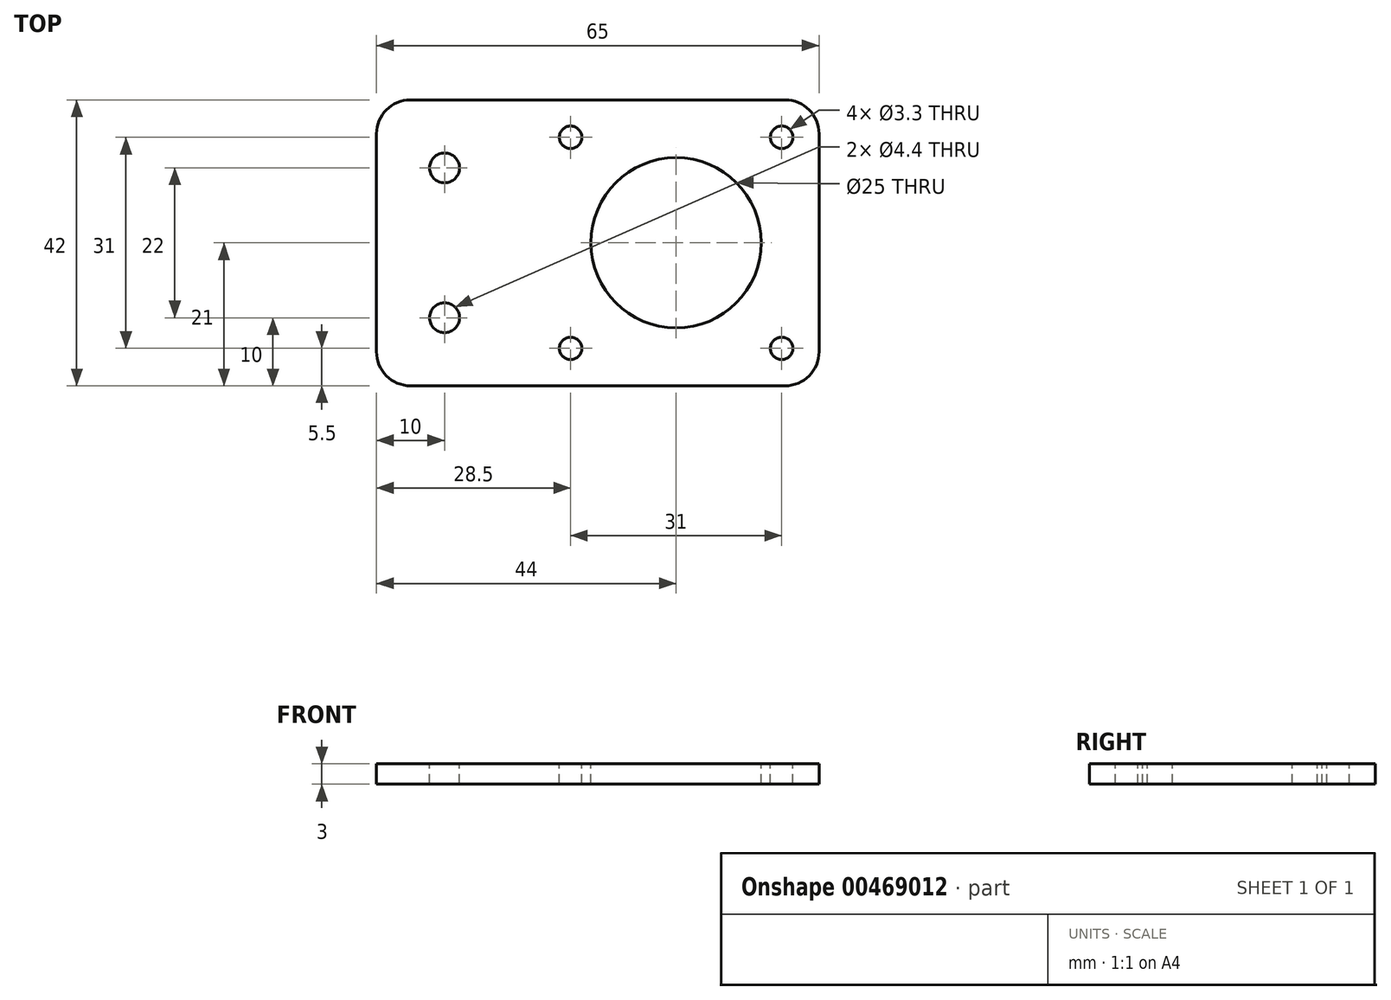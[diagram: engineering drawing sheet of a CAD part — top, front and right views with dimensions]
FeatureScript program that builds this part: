
annotation { "Feature Type Name" : "Feature", "Feature Type Description" : "" }
export const myFeature = defineFeature(function(context is Context, id is Id, definition is map)
    precondition{}
    {
        {
            var Q0;
            Q0=qCreatedBy(makeId("Top.planeOp"),FACE);
            var sketch = newSketch(context, id + "F0", { "sketchPlane" : qUnion([Q0])});
            skLineSegment(sketch, "E0.bottom", {"start": v(0, 0) * mm, "end": v(65, 0) * mm});
            skLineSegment(sketch, "E0.top", {"start": v(0, -42) * mm, "end": v(65, -42) * mm});
            skLineSegment(sketch, "E0.left", {"start": v(0, 0) * mm, "end": v(0, -42) * mm});
            skLineSegment(sketch, "E0.right", {"start": v(65, 0) * mm, "end": v(65, -42) * mm});
            skSolve(sketch);
        }
        {
            var Q0;
            Q0=makeQuery(id+"F0.imprint","IMPRINT",FACE,{"disambiguationData":[TD([[makeQuery(id+"F0.imprint","IMPRINT",EDGE,{"derivedFrom":sQuery(id+"F0.wireOp",EDGE,"E0.bottom")}),-1.0]])]});
            extrude(context, id + "F1", {"entities" : qUnion([Q0]), "depth" : 3 * mm});
        }
        {
            var Q0;
            Q0=makeQuery(id+"F1.opExtrude","CAP_FACE",FACE,{"disambiguationData":[OSD([sQuery(id+"F0.wireOp",EDGE,"E0.bottom"),sQuery(id+"F0.wireOp",EDGE,"E0.top"),sQuery(id+"F0.wireOp",EDGE,"E0.left"),sQuery(id+"F0.wireOp",EDGE,"E0.right")])],"isStart":false});
            var sketch = newSketch(context, id + "F2", { "sketchPlane" : qUnion([Q0])});
            skLineSegment(sketch, "E1", {"start": v(65, -21) * mm, "end": v(44, -21) * mm, "construction": true});
            skLineSegment(sketch, "E2", {"start": v(44, -21) * mm, "end": v(44, 0) * mm, "construction": true});
            skLineSegment(sketch, "E3", {"start": v(10, 0) * mm, "end": v(10, -42) * mm, "construction": true});
            skPoint(sketch, "E4", {"position": v(10, -10) * mm});
            skPoint(sketch, "E5.MirrorP", {"position": v(10, -32) * mm});
            skLineSegment(sketch, "E6.bottom", {"start": v(59.5, -5.5) * mm, "end": v(28.5, -5.5) * mm, "construction": true});
            skLineSegment(sketch, "E6.top", {"start": v(59.5, -36.5) * mm, "end": v(28.5, -36.5) * mm, "construction": true});
            skLineSegment(sketch, "E6.left", {"start": v(59.5, -5.5) * mm, "end": v(59.5, -36.5) * mm, "construction": true});
            skLineSegment(sketch, "E6.right", {"start": v(28.5, -5.5) * mm, "end": v(28.5, -36.5) * mm, "construction": true});
            skPoint(sketch, "E6.middle", {"position": v(44, -21) * mm});
            skSolve(sketch);
        }
        {
            var Q0;
            Q0=sQuery(id+"F2.wireOp",VERTEX,"E6.right.start");
            var Q1;
            Q1=sQuery(id+"F2.wireOp",VERTEX,"E6.right.end");
            var Q2;
            Q2=sQuery(id+"F2.wireOp",VERTEX,"E6.left.end");
            var Q3;
            Q3=sQuery(id+"F2.wireOp",VERTEX,"E6.bottom.start");
            var Q4;
            Q4=makeQuery(id+"F1.opExtrude","SWEPT_BODY",BODY,{"disambiguationData":[OSD([sQuery(id+"F0.wireOp",EDGE,"E0.bottom"),sQuery(id+"F0.wireOp",EDGE,"E0.top"),sQuery(id+"F0.wireOp",EDGE,"E0.left"),sQuery(id+"F0.wireOp",EDGE,"E0.right")])]});
            hole(context, id + "F3", {"style" : HoleStyle.SIMPLE, "endStyle" : HoleEndStyle.THROUGH, "standardTappedOrClearance" : lookupTablePath({ "standard" : "ISO", "fit" : "Normal", "size" : "M3", "type" : "Clearance" }), "standardBlindInLast" : lookupTablePath({ "fit" : "Standard", "standard" : "ISO", "size" : "M3", "type" : "Clearance" }), "holeDiameter" : 3.3 * mm, "isTappedThrough" : true, "tappedDepth" : 12 * mm, "tapClearance" : 3, "locations" : qUnion([Q0, Q1, Q2, Q3]), "scope" : qUnion([Q4])});
        }
        {
            var Q0;
            Q0=sQuery(id+"F2.wireOp",VERTEX,"E4");
            var Q1;
            Q1=sQuery(id+"F2.wireOp",VERTEX,"E5.MirrorP");
            var Q2;
            Q2=makeQuery(id+"F1.opExtrude","SWEPT_BODY",BODY,{"disambiguationData":[OSD([sQuery(id+"F0.wireOp",EDGE,"E0.bottom"),sQuery(id+"F0.wireOp",EDGE,"E0.top"),sQuery(id+"F0.wireOp",EDGE,"E0.left"),sQuery(id+"F0.wireOp",EDGE,"E0.right")])]});
            hole(context, id + "F4", {"style" : HoleStyle.SIMPLE, "endStyle" : HoleEndStyle.THROUGH, "standardTappedOrClearance" : lookupTablePath({ "standard" : "ISO", "fit" : "Normal", "size" : "M4", "type" : "Clearance" }), "standardBlindInLast" : lookupTablePath({ "fit" : "Standard", "standard" : "ISO", "size" : "M4", "type" : "Clearance" }), "holeDiameter" : 4.4 * mm, "isTappedThrough" : true, "tappedDepth" : 12 * mm, "tapClearance" : 3, "locations" : qUnion([Q0, Q1]), "scope" : qUnion([Q2])});
        }
        {
            var Q0;
            Q0=sQuery(id+"F2.wireOp",VERTEX,"E6.middle");
            var Q1;
            Q1=makeQuery(id+"F1.opExtrude","SWEPT_BODY",BODY,{"disambiguationData":[OSD([sQuery(id+"F0.wireOp",EDGE,"E0.bottom"),sQuery(id+"F0.wireOp",EDGE,"E0.top"),sQuery(id+"F0.wireOp",EDGE,"E0.left"),sQuery(id+"F0.wireOp",EDGE,"E0.right")])]});
            hole(context, id + "F5", {"style" : HoleStyle.SIMPLE, "endStyle" : HoleEndStyle.THROUGH, "holeDiameter" : 25 * mm, "isTappedThrough" : true, "tappedDepth" : 12 * mm, "tapClearance" : 3, "locations" : qUnion([Q0]), "scope" : qUnion([Q1])});
        }
        {
            var Q0;
            Q0=makeQuery(id+"F1.opExtrude","SWEPT_EDGE",EDGE,{"disambiguationData":[OSD([sQuery(id+"F0.wireOp",EDGE,"E0.top"),sQuery(id+"F0.wireOp",EDGE,"E0.left")])]});
            var Q1;
            Q1=makeQuery(id+"F1.opExtrude","SWEPT_EDGE",EDGE,{"disambiguationData":[OSD([sQuery(id+"F0.wireOp",EDGE,"E0.top"),sQuery(id+"F0.wireOp",EDGE,"E0.right")])]});
            var Q2;
            Q2=makeQuery(id+"F1.opExtrude","SWEPT_EDGE",EDGE,{"disambiguationData":[OSD([sQuery(id+"F0.wireOp",EDGE,"E0.bottom"),sQuery(id+"F0.wireOp",EDGE,"E0.right")])]});
            var Q3;
            Q3=makeQuery(id+"F1.opExtrude","SWEPT_EDGE",EDGE,{"disambiguationData":[OSD([sQuery(id+"F0.wireOp",EDGE,"E0.bottom"),sQuery(id+"F0.wireOp",EDGE,"E0.left")])]});
            fillet(context, id + "F6", {"entities" : qUnion([Q0, Q1, Q2, Q3]), "radius" : 5 * mm, "tangentPropagation" : true, "allowEdgeOverflow" : false});
        }
    });
